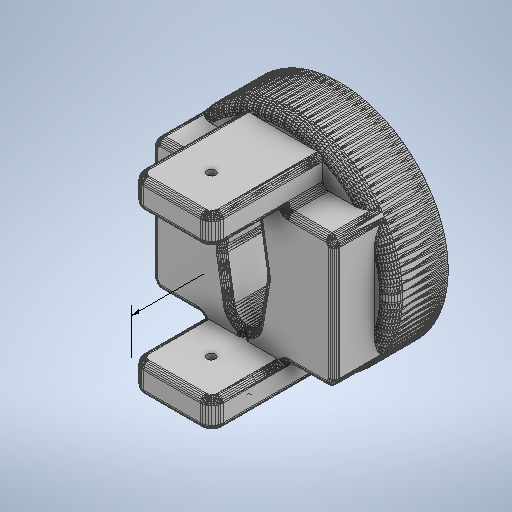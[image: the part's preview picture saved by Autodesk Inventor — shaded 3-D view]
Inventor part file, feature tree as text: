
AUTODESK INVENTOR PART (.ipt)
format: ipt  version: 2025 (Build 290162000, 162)  size: 12,723,712 bytes
history: native  units: in
note: dims shown in document units (in); Inventor stores cm internally (conversion verified against a paired STEP export)
features: other x6, sketch x3, extrude x2, direct_edit x2, pattern_circular x1, hole x1
ambient origin geometry x8: Origin, YZ Plane, XZ Plane, XY Plane, X Axis, Y Axis, Z Axis, Center Point
bodies: Solid1 (feature_tree)
feature tree (15):
  other  "Annotations"
  other  "top"
  other  "MeshFeature1"
  pattern_circular  "Circular Pattern1"  Count=2 Angle=360.0deg
  extrude  "Extrusion1"  Depth=1.5in
  extrude  "Extrusion2"  Depth=1.5in
  hole  "Hole1"  [1 undecoded]
  direct_edit  "Direct Edit1"
  direct_edit  "Direct Edit2"
  sketch  "Sketch2"  dims[d4=1.5in d5=1.5in]
  sketch  "Sketch3"  dims[d6=13.9961in d7=0.0in d8=1.5in]
  sketch  "Sketch4"  dims[d9=13.9961in d10=0.0in d11=1.5in d12=0.2362in d13=0.1575in d14=0.0787in d15=90.0deg d16=0.315in d17=0.8108in d21=0.1607in d22=0.3937in d23=0.3937in d24=0.038in d25=0.3937in d26=0.3937in d18=0.2701in d19=0.0749in d20=1.1614in]
  other  "Scale1"
  other  "Scale2"
  other  "Linear Dimension 1"
note: 1 required parameter value undecoded (feature->parameter linkage not recoverable at this tier; creation-order binding heuristic only, values carry confidence <= 0.55)
